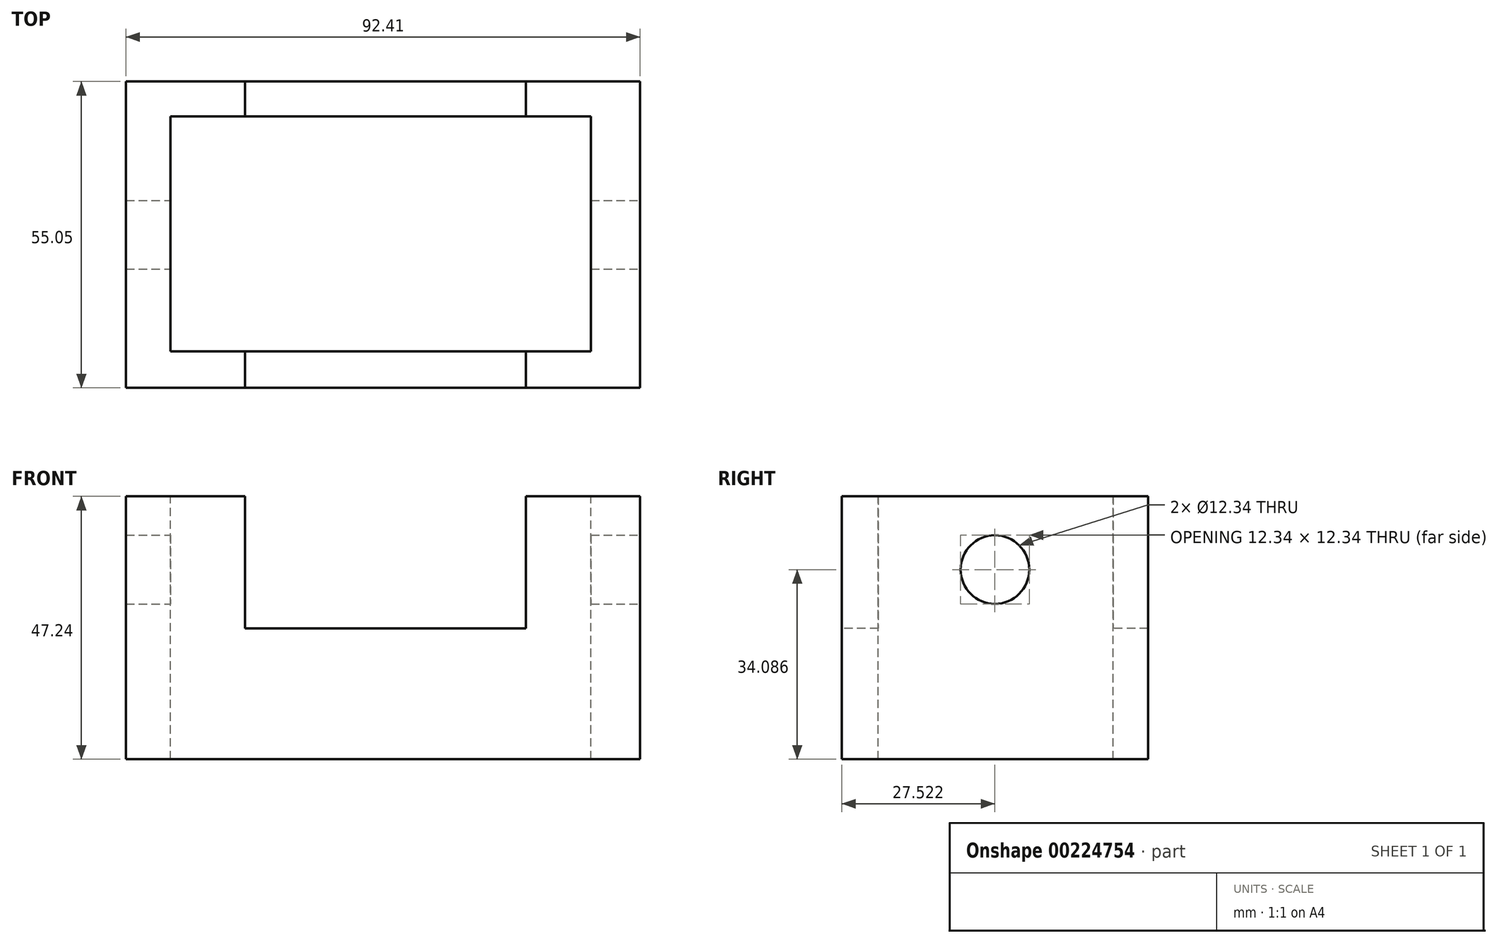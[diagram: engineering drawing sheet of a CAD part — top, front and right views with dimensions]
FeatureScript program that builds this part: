
annotation { "Feature Type Name" : "Feature", "Feature Type Description" : "" }
export const myFeature = defineFeature(function(context is Context, id is Id, definition is map)
    precondition{}
    {
        {
            var Q0;
            Q0=qCreatedBy(makeId("Top.planeOp"),FACE);
            var sketch = newSketch(context, id + "F0", { "sketchPlane" : qUnion([Q0])});
            skLineSegment(sketch, "E0.bottom", {"start": v(-39.93, 30.38) * mm, "end": v(52.48, 30.38) * mm});
            skLineSegment(sketch, "E0.top", {"start": v(-39.93, -24.67) * mm, "end": v(52.48, -24.67) * mm});
            skLineSegment(sketch, "E0.left", {"start": v(-39.93, 30.38) * mm, "end": v(-39.93, -24.67) * mm});
            skLineSegment(sketch, "E0.right", {"start": v(52.48, 30.38) * mm, "end": v(52.48, -24.67) * mm});
            skSolve(sketch);
        }
        {
            var Q0;
            Q0=makeQuery(id+"F0.imprint","IMPRINT",FACE,{"disambiguationData":[TD([[makeQuery(id+"F0.imprint","IMPRINT",EDGE,{"derivedFrom":sQuery(id+"F0.wireOp",EDGE,"E0.bottom")}),-1.0]])]});
            extrude(context, id + "F1", {"entities" : qUnion([Q0]), "depth" : 47.24 * mm});
        }
        {
            var Q0;
            Q0=makeQuery(id+"F1.opExtrude","CAP_FACE",FACE,{"disambiguationData":[OSD([sQuery(id+"F0.wireOp",EDGE,"E0.bottom"),sQuery(id+"F0.wireOp",EDGE,"E0.top"),sQuery(id+"F0.wireOp",EDGE,"E0.left"),sQuery(id+"F0.wireOp",EDGE,"E0.right")])],"isStart":false});
            var sketch = newSketch(context, id + "F2", { "sketchPlane" : qUnion([Q0])});
            skLineSegment(sketch, "E1.bottom", {"start": v(-31.95, 24.1) * mm, "end": v(43.64, 24.1) * mm});
            skLineSegment(sketch, "E1.top", {"start": v(-31.95, -18.11) * mm, "end": v(43.64, -18.11) * mm});
            skLineSegment(sketch, "E1.left", {"start": v(-31.95, 24.1) * mm, "end": v(-31.95, -18.11) * mm});
            skLineSegment(sketch, "E1.right", {"start": v(43.64, 24.1) * mm, "end": v(43.64, -18.11) * mm});
            skSolve(sketch);
        }
        {
            var Q0;
            Q0=makeQuery(id+"F2.imprint","IMPRINT",FACE,{"disambiguationData":[TD([[makeQuery(id+"F2.imprint","IMPRINT",EDGE,{"derivedFrom":sQuery(id+"F2.wireOp",EDGE,"E1.bottom")}),-1.0]])]});
            extrude(context, id + "F3", {"entities" : qUnion([Q0]), "operationType" : NewBodyOperationType.REMOVE, "endBound" : BoundingType.THROUGH_ALL, "oppositeDirection" : true, "depth" : 25.4 * mm});
        }
        {
            var Q0;
            Q0=makeQuery(id+"F1.opExtrude","SWEPT_FACE",FACE,{"disambiguationData":[OSD([sQuery(id+"F0.wireOp",EDGE,"E0.top")])]});
            var sketch = newSketch(context, id + "F4", { "sketchPlane" : qUnion([Q0])});
            skLineSegment(sketch, "E2.bottom", {"start": v(-18.54, 47.24) * mm, "end": v(31.95, 47.24) * mm});
            skLineSegment(sketch, "E2.top", {"start": v(-18.54, 23.53) * mm, "end": v(31.95, 23.53) * mm});
            skLineSegment(sketch, "E2.left", {"start": v(-18.54, 47.24) * mm, "end": v(-18.54, 23.53) * mm});
            skLineSegment(sketch, "E2.right", {"start": v(31.95, 47.24) * mm, "end": v(31.95, 23.53) * mm});
            skSolve(sketch);
        }
        {
            var Q0;
            Q0=makeQuery(id+"F4.imprint","IMPRINT",FACE,{"disambiguationData":[TD([[makeQuery(id+"F4.imprint","IMPRINT",EDGE,{"derivedFrom":sQuery(id+"F4.wireOp",EDGE,"E2.bottom")}),-1.0]])]});
            extrude(context, id + "F5", {"entities" : qUnion([Q0]), "operationType" : NewBodyOperationType.REMOVE, "endBound" : BoundingType.THROUGH_ALL, "oppositeDirection" : true, "depth" : 54.86 * mm});
        }
        {
            var Q0;
            Q0=makeQuery(id+"F1.opExtrude","SWEPT_FACE",FACE,{"disambiguationData":[OSD([sQuery(id+"F0.wireOp",EDGE,"E0.right")])]});
            var sketch = newSketch(context, id + "F6", { "sketchPlane" : qUnion([Q0])});
            skCircle(sketch, "E3", {"center": v(2.85, 34.09) * mm, "radius": 6.17 * mm});
            skSolve(sketch);
        }
        {
            var Q0;
            Q0=makeQuery(id+"F6.imprint","IMPRINT",FACE,{"disambiguationData":[TD([[makeQuery(id+"F6.imprint","IMPRINT",EDGE,{"derivedFrom":sQuery(id+"F6.wireOp",EDGE,"E3")}),1.0]])]});
            extrude(context, id + "F7", {"entities" : qUnion([Q0]), "operationType" : NewBodyOperationType.REMOVE, "endBound" : BoundingType.THROUGH_ALL, "oppositeDirection" : true, "depth" : 25.4 * mm});
        }
    });
